# Revit family: MIFAB-R1500
name_source: partatom
category: Pipe Accessories
units: mm (PartAtom-declared; Revit-internal decimal feet)

## family parameters
Always vertical = No
Cut with Voids When Loaded = No
Part Type = Normal
Round Connector Dimension = Use Diameter
Shared = No
Work Plane-Based = No

## types (5) — shared parameters
DIA = 4.00"
Default Elevation = 0.00"
Description = DOWNSPOUT BOOTS
Manufacturer = MIFAB
Pipe size = 4.00"
Pipe size inner = 3.50"
URL = WWW.MIFAB.COM

## per-type parameters (varying)
| type | Body depth | Body width | Holes to receive | Length | Offset | Type circle | Type rectangular |
| R1530 | 3.00" | 4.00" | 6.13" | 18.00" | 1.00" | Yes | No |
| R1510-18 | 3.00" | 4.00" | 5.63" | 18.00" | 0.50" | No | Yes |
| R1510-24 | 3.00" | 4.00" | 5.63" | 24.00" | 0.50" | No | Yes |
| R1510-12 | 3.00" | 4.00" | 5.63" | 12.00" | 0.50" | No | Yes |
| R1520 | 4.00" | 5.00" | 6.63" | 24.00" | 1.00" | No | Yes |

note: column(s) folded — value = type name in every type: Model

## geometry (parser evidence)
native form markers: Sweep x7
no freeform markers — native parametric forms only
